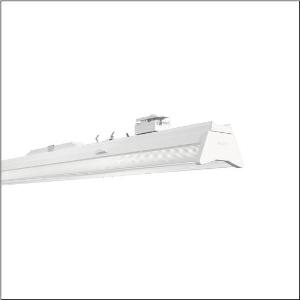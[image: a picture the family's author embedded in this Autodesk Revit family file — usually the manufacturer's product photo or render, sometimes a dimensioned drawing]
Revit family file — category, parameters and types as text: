
# Revit family: licross_r__21_performance_mo_52td16vn48xg_2cf7
name_source: partatom
category: Lighting Fixtures
units: mm (PartAtom-declared; Revit-internal decimal feet)

## family parameters
Cut with Voids When Loaded = No
Host = Face
Light Source = No
Part Type = Normal
Room Calculation Point = No
Round Connector Dimension = Use Diameter
Shared = No

## types (1)
- --- (1 x LED, 8000 lm, 44.6 W, 4000K)
    Apparent Load = 45 VA
    CIE Flux Codes = 66 88 96 79 100
    Color Rendering = 80
    Color Temperature = 4000K
    Default Elevation = 1800 mm
    Description = Licross® 21 Performance MO, luminaire insert, of sheet steel, galvanised, coil coated, white, length: 1.500mm, width: 120mm, height: 123mm, LED rated luminous flux: 8.000lm, light colour: 840, control gear: DALI 2, CLO, with plug, 5-pole, with phase selection, mains connection: 220..240V, AC, 50/60Hz, start of lifetime: 45W, end of service life: 53W, halogen-free wiring, primary light control with lens, of plastic, primary optical cover: cover, of PMMA, light emission: direct/indirect distribution, primary light characteristic: symmetric, protection rating (complete): IP54, insulation class (complete): insulation class I (protective earthing), certification: CE, ENEC, VDE, UKCA, protection symbol: D if used in an environment with non-conductive dust loads with corresponding accessories, impact resistance: IK06, permissible ambient temperature for indoor applications: -25..+45°C, corresponds to IFS (International Featured Standards) requirements for safety and quality in the food industry, reducing of maximum allowable ambient temperature of 5°C with ceiling mounting, LABS conformity tested according to VDMA 24364:2018-05, packaging unit: 1 piece
    Height = 114 mm
    Lamp = 1 x LED
    Lamp Light Flux = 8000 lm
    Lamp Power = 44.6 W
    Lamp count = 1
    Length = 1500 mm
    Luminous efficacy = 179 lm/W
    Manufacturer = Siteco
    ModVariant = No
    Model = 52TD16VN48XG
    Mounting Place = Ceiling
    Mounting Type = Pendant
    Number of Poles = 1
    OnlyDefault = Yes
    Power Factor = 1
    Product Name = Licross® 21 Performance MO
    Product group = luminaire insert
    ProductGroupID = 901
    Protection Class = Protection class I
    Protection Degree = IP 54
    RLX_Detail_Level = 1
    RLX_Emergency_Light_Flux = 0 lm
    RLX_Emergency_Type = 0
    RLX_Emergency_Type_DB = No
    RlxData = <blob elided: 34009 chars, md5=3f980b29>
    Socket = socket
    Standby Power = 0 W
    System Light Flux = 8000 lm
    System Power = 45 W
    Type Comments = factory setting: luminous flux: 100 % | dim-lin: 254 | 301 mA
    Type Image = l_1256138.jpg
    URL = http://relux.com
    VarID = @adj_035419
    Voltage = 0 V
    Weight = 0.00 kg
    Width = 120 mm

## geometry (parser evidence)
native form markers: Blend x4, Sweep x12
no freeform markers — native parametric forms only
